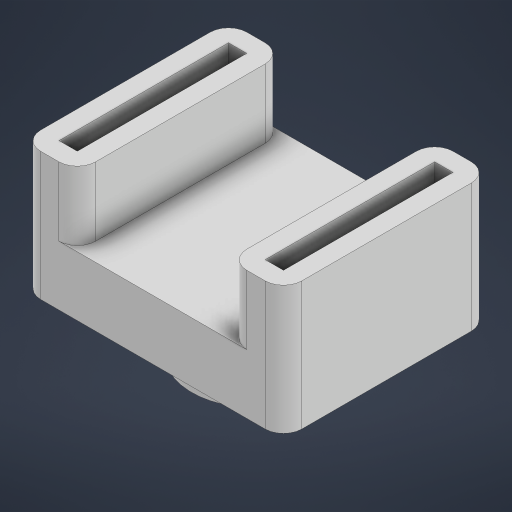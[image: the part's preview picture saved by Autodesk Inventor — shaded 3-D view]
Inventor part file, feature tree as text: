
AUTODESK INVENTOR PART (.ipt)
format: ipt  version: 2023 (Build 270158030, 158C)  size: 244,736 bytes
history: native  units: mm
features: sketch x3, extrude x2, revolve x1, fillet x1, projected_geometry x1
ambient origin geometry x8: Origin, YZ Plane, XZ Plane, XY Plane, X Axis, Y Axis, Z Axis, Center Point
bodies: Solid1 (feature_tree)
feature tree (8):
  revolve  "Revolution1"  [1 undecoded]
  extrude  "Extrusion1"  Depth=4.3mm
  fillet  "Fillet1"  [1 undecoded]
  extrude  "Extrusion2"  Depth=22.5mm
  sketch  "Sketch1"  dims[d0=7.0mm d1=7.0mm]
  sketch  "Sketch2"  dims[d2=1.05mm d3=4.3mm d4=90.0deg]
  sketch  "Sketch3"  dims[d5=28.5mm d6=22.5mm d7=6.5mm d8=0.0mm d9=2.0mm d10=6.0mm d11=2.0mm d12=2.0mm d13=2.0mm d14=7.5mm d15=0.0mm]
  projected_geometry  "Projected Loop1"
note: 2 required parameter values undecoded (feature->parameter linkage not recoverable at this tier; creation-order binding heuristic only, values carry confidence <= 0.55)